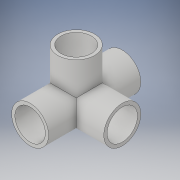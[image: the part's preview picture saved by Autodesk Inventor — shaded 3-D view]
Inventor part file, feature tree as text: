
AUTODESK INVENTOR PART (.ipt)
format: ipt  version: 2018 (Build 220112000, 112)  size: 183,808 bytes
history: native  units: in
note: dims shown in document units (in); Inventor stores cm internally (conversion verified against a paired STEP export)
features: sketch x14, extrude x12, plane x2
ambient origin geometry x8: Origin, YZ Plane, XZ Plane, XY Plane, X Axis, Y Axis, Z Axis, Center Point
bodies: Solid1 (feature_tree)
feature tree (28):
  extrude  "Extrusion1"  Depth=4.0in TaperAngle=0.0deg
  sketch  "Sketch11"
  sketch  "Sketch10"  dims[d29=1.0in d30=2.0in d31=0.0in]
  sketch  "Sketch2"  dims[d3=1.1975in d4=0.0in d5=0.8025in d6=0.0in]
  sketch  "Sketch3"  dims[d7=1.321in d8=1.0in]
  plane  "Work Plane1"
  plane  "Work Plane2"
  sketch  "Sketch4"  dims[d9=1.321in d10=1.0in]
  extrude  "Extrusion2"  Depth=0.8025in TaperAngle=0.0deg
  extrude  "Extrusion3"  Depth=1.0in
  sketch  "Sketch12"
  extrude  "Extrusion9"  Depth=1.0in
  extrude  "Extrusion10"  Depth=1.25in TaperAngle=0.0deg
  sketch  "Sketch5"  dims[d11=1.321in d12=1.25in d13=0.0in]
  sketch  "Sketch6"  dims[d14=1.25in d15=0.0in d16=1.25in d17=0.0in]
  sketch  "Sketch7"  dims[d18=4.0in d19=0.0in d20=2.0in d21=0.0in]
  sketch  "Sketch8"  dims[d22=1.1975in d23=0.0in d24=0.8025in d25=0.0in]
  extrude  "Extrusion4"  Depth=1.25in TaperAngle=0.0deg
  extrude  "Extrusion5"  Depth=4.0in TaperAngle=0.0deg
  extrude  "Extrusion6"  Depth=0.8025in TaperAngle=0.0deg
  extrude  "Extrusion7"  Depth=1.25in TaperAngle=0.0deg
  extrude  "Extrusion8"  Depth=2.0in TaperAngle=0.0deg
  extrude  "Extrusion11"  [1 undecoded]
  extrude  "Extrusion12"  [1 undecoded]
  sketch  "Sketch1"  dims[d0=1.605in d1=4.0in d2=0.0in]
  sketch  "Sketch9"  dims[d26=1.321in d27=1.25in d28=0.0in]
  sketch  "Sketch13"
  sketch  "Sketch14"
note: 2 required parameter values undecoded (feature->parameter linkage not recoverable at this tier; creation-order binding heuristic only, values carry confidence <= 0.55)
